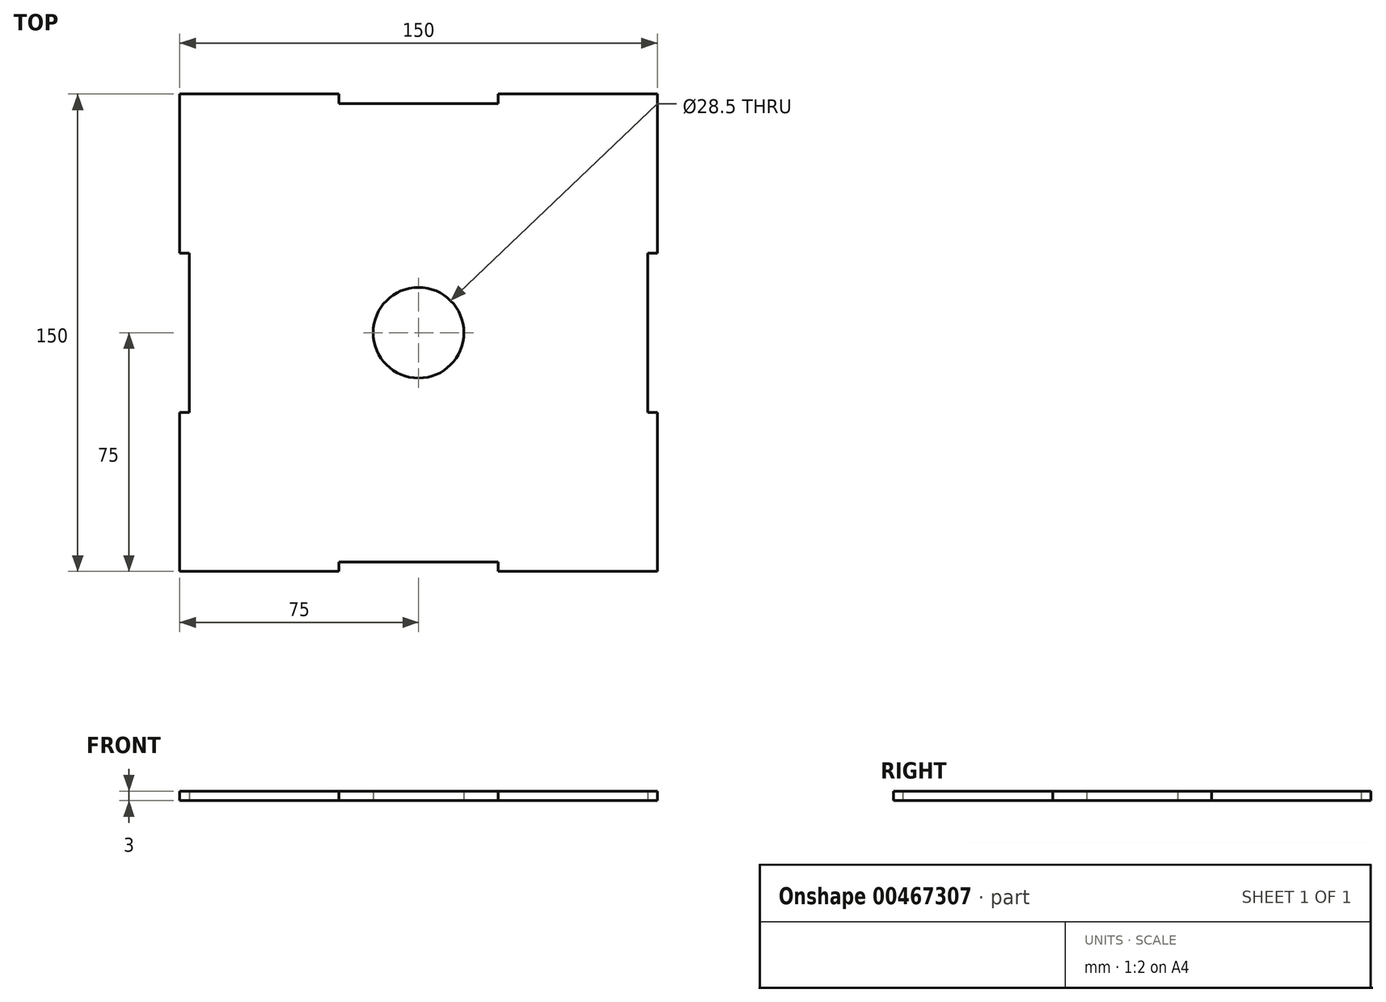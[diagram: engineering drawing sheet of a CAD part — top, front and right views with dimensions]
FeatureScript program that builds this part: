
annotation { "Feature Type Name" : "Feature", "Feature Type Description" : "" }
export const myFeature = defineFeature(function(context is Context, id is Id, definition is map)
    precondition{}
    {
        {
            var Q0;
            Q0=qCreatedBy(makeId("Top.planeOp"),FACE);
            var sketch = newSketch(context, id + "F0", { "sketchPlane" : qUnion([Q0])});
            skLineSegment(sketch, "E0.bottom", {"start": v(75, 75) * mm, "end": v(25, 75) * mm});
            skLineSegment(sketch, "E0.top", {"start": v(75, -75) * mm, "end": v(25, -75) * mm});
            skLineSegment(sketch, "E0.left", {"start": v(75, 75) * mm, "end": v(75, 25) * mm});
            skLineSegment(sketch, "E0.right", {"start": v(-75, 75) * mm, "end": v(-75, 25) * mm});
            skPoint(sketch, "E0.middle", {"position": v(0, 0) * mm});
            skLineSegment(sketch, "E1", {"start": v(-75, 25) * mm, "end": v(-72, 25) * mm});
            skLineSegment(sketch, "E2", {"start": v(-72, 25) * mm, "end": v(-72, -25) * mm});
            skLineSegment(sketch, "E3", {"start": v(-72, -25) * mm, "end": v(-75, -25) * mm});
            skLineSegment(sketch, "E4.trimOffspring", {"start": v(-75, -25) * mm, "end": v(-75, -75) * mm});
            skLineSegment(sketch, "E5", {"start": v(-75, 75) * mm, "end": v(-25, 75) * mm});
            skLineSegment(sketch, "E6", {"start": v(-25, 75) * mm, "end": v(-25, 72) * mm});
            skLineSegment(sketch, "E7", {"start": v(-25, 72) * mm, "end": v(25, 72) * mm});
            skLineSegment(sketch, "E8", {"start": v(25, 72) * mm, "end": v(25, 75) * mm});
            skLineSegment(sketch, "E9.trimOffspring", {"start": v(-25, 75) * mm, "end": v(-75, 75) * mm});
            skLineSegment(sketch, "E10", {"start": v(75, 25) * mm, "end": v(72, 25) * mm});
            skLineSegment(sketch, "E11", {"start": v(72, 25) * mm, "end": v(72, -25) * mm});
            skLineSegment(sketch, "E12", {"start": v(72, -25) * mm, "end": v(75, -25) * mm});
            skLineSegment(sketch, "E13.trimOffspring", {"start": v(75, -25) * mm, "end": v(75, -75) * mm});
            skLineSegment(sketch, "E14", {"start": v(-75, -75) * mm, "end": v(-25, -75) * mm});
            skLineSegment(sketch, "E15", {"start": v(-25, -75) * mm, "end": v(-25, -72) * mm});
            skLineSegment(sketch, "E16", {"start": v(-25, -72) * mm, "end": v(25, -72) * mm});
            skLineSegment(sketch, "E17", {"start": v(25, -72) * mm, "end": v(25, -75) * mm});
            skLineSegment(sketch, "E18.trimOffspring", {"start": v(-25, -75) * mm, "end": v(-75, -75) * mm});
            skCircle(sketch, "E19", {"center": v(0, 0) * mm, "radius": 14.25 * mm});
            skSolve(sketch);
        }
        {
            var Q0;
            Q0=makeQuery(id+"F0.imprint","IMPRINT",FACE,{"disambiguationData":[TD([[makeQuery(id+"F0.imprint","IMPRINT",EDGE,{"derivedFrom":sQuery(id+"F0.wireOp",EDGE,"E0.bottom")}),1.0]])]});
            extrude(context, id + "F1", {"entities" : qUnion([Q0]), "depth" : 3 * mm});
        }
    });
